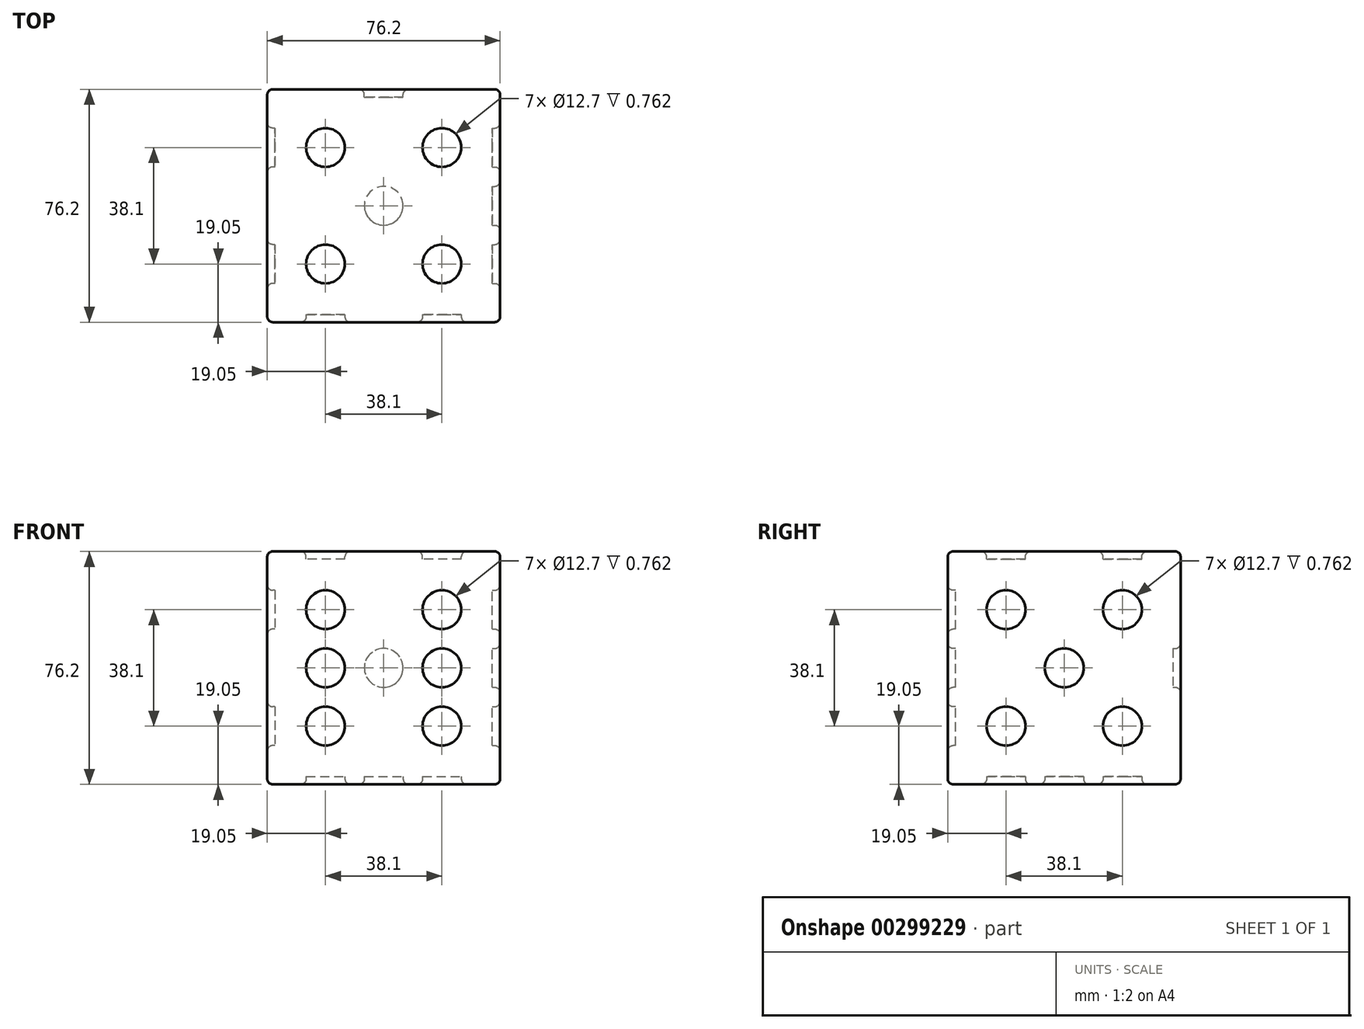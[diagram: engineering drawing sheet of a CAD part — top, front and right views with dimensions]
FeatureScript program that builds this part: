
annotation { "Feature Type Name" : "Feature", "Feature Type Description" : "" }
export const myFeature = defineFeature(function(context is Context, id is Id, definition is map)
    precondition{}
    {
        {
            var Q0;
            Q0=qCreatedBy(makeId("Top.planeOp"),FACE);
            var sketch = newSketch(context, id + "F0", { "sketchPlane" : qUnion([Q0])});
            skLineSegment(sketch, "E0.bottom", {"start": v(38.1, -38.1) * mm, "end": v(-38.1, -38.1) * mm});
            skLineSegment(sketch, "E0.top", {"start": v(38.1, 38.1) * mm, "end": v(-38.1, 38.1) * mm});
            skLineSegment(sketch, "E0.left", {"start": v(38.1, -38.1) * mm, "end": v(38.1, 38.1) * mm});
            skLineSegment(sketch, "E0.right", {"start": v(-38.1, -38.1) * mm, "end": v(-38.1, 38.1) * mm});
            skPoint(sketch, "E0.middle", {"position": v(0, 0) * mm});
            skSolve(sketch);
        }
        {
            var Q0;
            Q0 = qSketchRegion(id + "F0", true);
            extrude(context, id + "F1", {"entities" : qUnion([Q0]), "depth" : 38.1 * mm});
        }
        {
            var Q0;
            Q0 = qSketchRegion(id + "F0", true);
            extrude(context, id + "F2", {"entities" : qUnion([Q0]), "operationType" : NewBodyOperationType.ADD, "oppositeDirection" : true, "depth" : 38.1 * mm});
        }
        {
            var Q0;
            {var subQ0=sQuery(id+"F0.wireOp",EDGE,"E0.bottom");Q0=makeQuery(id+"F2.boolean.opBoolean","MERGE",FACE,{"derivedFrom":[makeQuery(id+"F1.opExtrude","SWEPT_FACE",FACE,{"disambiguationData":[OSD([subQ0])]}),makeQuery(id+"F2.opExtrude","SWEPT_FACE",FACE,{"disambiguationData":[OSD([subQ0])]})]});}
            var sketch = newSketch(context, id + "F3", { "sketchPlane" : qUnion([Q0])});
            skCircle(sketch, "E1", {"center": v(19.05, 19.05) * mm, "radius": 6.35 * mm});
            skCircle(sketch, "E2", {"center": v(-19.05, 19.05) * mm, "radius": 6.35 * mm});
            skCircle(sketch, "E3", {"center": v(-19.05, 0) * mm, "radius": 6.35 * mm});
            skCircle(sketch, "E4", {"center": v(19.05, 0) * mm, "radius": 6.35 * mm});
            skCircle(sketch, "E5", {"center": v(19.05, -19.05) * mm, "radius": 6.35 * mm});
            skCircle(sketch, "E6", {"center": v(-19.05, -19.05) * mm, "radius": 6.35 * mm});
            skSolve(sketch);
        }
        {
            var Q0;
            {var subQ0=sQuery(id+"F0.wireOp",EDGE,"E0.top");Q0=makeQuery(id+"F2.boolean.opBoolean","MERGE",FACE,{"derivedFrom":[makeQuery(id+"F1.opExtrude","SWEPT_FACE",FACE,{"disambiguationData":[OSD([subQ0])]}),makeQuery(id+"F2.opExtrude","SWEPT_FACE",FACE,{"disambiguationData":[OSD([subQ0])]})]});}
            var sketch = newSketch(context, id + "F4", { "sketchPlane" : qUnion([Q0])});
            skCircle(sketch, "E7", {"center": v(0, 0) * mm, "radius": 6.35 * mm});
            skSolve(sketch);
        }
        {
            var Q0;
            {var subQ0=sQuery(id+"F0.wireOp",EDGE,"E0.right");Q0=makeQuery(id+"F2.boolean.opBoolean","MERGE",FACE,{"derivedFrom":[makeQuery(id+"F1.opExtrude","SWEPT_FACE",FACE,{"disambiguationData":[OSD([subQ0])]}),makeQuery(id+"F2.opExtrude","SWEPT_FACE",FACE,{"disambiguationData":[OSD([subQ0])]})]});}
            var sketch = newSketch(context, id + "F5", { "sketchPlane" : qUnion([Q0])});
            skCircle(sketch, "E8", {"center": v(-19.05, 19.05) * mm, "radius": 6.35 * mm});
            skPoint(sketch, "E8.centerSnap0", {"position": v(0, 38.1) * mm});
            skCircle(sketch, "E9", {"center": v(19.05, -19.05) * mm, "radius": 6.35 * mm});
            skSolve(sketch);
        }
        {
            var Q0;
            {var subQ0=sQuery(id+"F0.wireOp",EDGE,"E0.left");Q0=makeQuery(id+"F2.boolean.opBoolean","MERGE",FACE,{"derivedFrom":[makeQuery(id+"F1.opExtrude","SWEPT_FACE",FACE,{"disambiguationData":[OSD([subQ0])]}),makeQuery(id+"F2.opExtrude","SWEPT_FACE",FACE,{"disambiguationData":[OSD([subQ0])]})]});}
            var sketch = newSketch(context, id + "F6", { "sketchPlane" : qUnion([Q0])});
            skCircle(sketch, "E10", {"center": v(19.05, 19.05) * mm, "radius": 6.35 * mm});
            skCircle(sketch, "E11", {"center": v(19.05, -19.05) * mm, "radius": 6.35 * mm});
            skCircle(sketch, "E12", {"center": v(0, 0) * mm, "radius": 6.35 * mm});
            skCircle(sketch, "E13", {"center": v(-19.05, -19.05) * mm, "radius": 6.35 * mm});
            skCircle(sketch, "E14", {"center": v(-19.05, 19.05) * mm, "radius": 6.35 * mm});
            skSolve(sketch);
        }
        {
            var Q0;
            Q0=makeQuery(id+"F2.opExtrude","CAP_FACE",FACE,{"disambiguationData":[OSD([sQuery(id+"F0.wireOp",EDGE,"E0.bottom"),sQuery(id+"F0.wireOp",EDGE,"E0.top"),sQuery(id+"F0.wireOp",EDGE,"E0.left"),sQuery(id+"F0.wireOp",EDGE,"E0.right")])],"isStart":false});
            var sketch = newSketch(context, id + "F7", { "sketchPlane" : qUnion([Q0])});
            skCircle(sketch, "E15", {"center": v(0, 0) * mm, "radius": 6.35 * mm});
            skCircle(sketch, "E16", {"center": v(-19.05, 19.05) * mm, "radius": 6.35 * mm});
            skCircle(sketch, "E17", {"center": v(19.05, -19.05) * mm, "radius": 6.35 * mm});
            skSolve(sketch);
        }
        {
            var Q0;
            Q0=makeQuery(id+"F1.opExtrude","CAP_FACE",FACE,{"disambiguationData":[OSD([sQuery(id+"F0.wireOp",EDGE,"E0.bottom"),sQuery(id+"F0.wireOp",EDGE,"E0.top"),sQuery(id+"F0.wireOp",EDGE,"E0.left"),sQuery(id+"F0.wireOp",EDGE,"E0.right")])],"isStart":false});
            var sketch = newSketch(context, id + "F8", { "sketchPlane" : qUnion([Q0])});
            skCircle(sketch, "E18", {"center": v(-19.05, -19.05) * mm, "radius": 6.35 * mm});
            skCircle(sketch, "E19", {"center": v(19.05, 19.05) * mm, "radius": 6.35 * mm});
            skCircle(sketch, "E20", {"center": v(-19.05, 19.05) * mm, "radius": 6.35 * mm});
            skCircle(sketch, "E21", {"center": v(19.05, -19.05) * mm, "radius": 6.35 * mm});
            skSolve(sketch);
        }
        {
            var Q0;
            Q0=makeQuery(id+"F8.imprint","IMPRINT",FACE,{"disambiguationData":[TD([[makeQuery(id+"F8.imprint","IMPRINT",EDGE,{"derivedFrom":sQuery(id+"F8.wireOp",EDGE,"E18")}),1.0]])]});
            var Q1;
            Q1=makeQuery(id+"F8.imprint","IMPRINT",FACE,{"disambiguationData":[TD([[makeQuery(id+"F8.imprint","IMPRINT",EDGE,{"derivedFrom":sQuery(id+"F8.wireOp",EDGE,"E19")}),1.0]])]});
            var Q2;
            Q2=makeQuery(id+"F8.imprint","IMPRINT",FACE,{"disambiguationData":[TD([[makeQuery(id+"F8.imprint","IMPRINT",EDGE,{"derivedFrom":sQuery(id+"F8.wireOp",EDGE,"E20")}),1.0]])]});
            var Q3;
            Q3=makeQuery(id+"F8.imprint","IMPRINT",FACE,{"disambiguationData":[TD([[makeQuery(id+"F8.imprint","IMPRINT",EDGE,{"derivedFrom":sQuery(id+"F8.wireOp",EDGE,"E21")}),1.0]])]});
            extrude(context, id + "F9", {"entities" : qUnion([Q0, Q1, Q2, Q3]), "operationType" : NewBodyOperationType.REMOVE, "oppositeDirection" : true, "depth" : 2.54 * mm});
        }
        {
            var Q0;
            Q0 = qSketchRegion(id + "F7", true);
            extrude(context, id + "F10", {"entities" : qUnion([Q0]), "operationType" : NewBodyOperationType.REMOVE, "oppositeDirection" : true, "depth" : 2.54 * mm});
        }
        {
            var Q0;
            Q0 = qSketchRegion(id + "F6", true);
            extrude(context, id + "F11", {"entities" : qUnion([Q0]), "operationType" : NewBodyOperationType.REMOVE, "oppositeDirection" : true, "depth" : 2.54 * mm});
        }
        {
            var Q0;
            Q0 = qSketchRegion(id + "F5", true);
            extrude(context, id + "F12", {"entities" : qUnion([Q0]), "operationType" : NewBodyOperationType.REMOVE, "oppositeDirection" : true, "depth" : 2.54 * mm});
        }
        {
            var Q0;
            Q0 = qSketchRegion(id + "F4", true);
            extrude(context, id + "F13", {"entities" : qUnion([Q0]), "operationType" : NewBodyOperationType.REMOVE, "oppositeDirection" : true, "depth" : 2.54 * mm});
        }
        {
            var Q0;
            Q0 = qSketchRegion(id + "F3", true);
            extrude(context, id + "F14", {"entities" : qUnion([Q0]), "operationType" : NewBodyOperationType.REMOVE, "oppositeDirection" : true, "depth" : 2.54 * mm});
        }
        {
            var Q0;
            Q0=makeQuery(id+"F2.opExtrude","CAP_FACE",FACE,{"disambiguationData":[OSD([sQuery(id+"F0.wireOp",EDGE,"E0.bottom"),sQuery(id+"F0.wireOp",EDGE,"E0.top"),sQuery(id+"F0.wireOp",EDGE,"E0.left"),sQuery(id+"F0.wireOp",EDGE,"E0.right")])],"isStart":false});
            var Q1;
            {var subQ0=sQuery(id+"F0.wireOp",EDGE,"E0.bottom");Q1=makeQuery(id+"F2.boolean.opBoolean","MERGE",FACE,{"derivedFrom":[makeQuery(id+"F1.opExtrude","SWEPT_FACE",FACE,{"disambiguationData":[OSD([subQ0])]}),makeQuery(id+"F2.opExtrude","SWEPT_FACE",FACE,{"disambiguationData":[OSD([subQ0])]})]});}
            var Q2;
            {var subQ0=sQuery(id+"F0.wireOp",EDGE,"E0.right");Q2=makeQuery(id+"F2.boolean.opBoolean","MERGE",FACE,{"derivedFrom":[makeQuery(id+"F1.opExtrude","SWEPT_FACE",FACE,{"disambiguationData":[OSD([subQ0])]}),makeQuery(id+"F2.opExtrude","SWEPT_FACE",FACE,{"disambiguationData":[OSD([subQ0])]})]});}
            var Q3;
            {var subQ0=sQuery(id+"F0.wireOp",EDGE,"E0.top");Q3=makeQuery(id+"F2.boolean.opBoolean","MERGE",FACE,{"derivedFrom":[makeQuery(id+"F1.opExtrude","SWEPT_FACE",FACE,{"disambiguationData":[OSD([subQ0])]}),makeQuery(id+"F2.opExtrude","SWEPT_FACE",FACE,{"disambiguationData":[OSD([subQ0])]})]});}
            var Q4;
            {var subQ0=sQuery(id+"F0.wireOp",EDGE,"E0.left");Q4=makeQuery(id+"F2.boolean.opBoolean","MERGE",FACE,{"derivedFrom":[makeQuery(id+"F1.opExtrude","SWEPT_FACE",FACE,{"disambiguationData":[OSD([subQ0])]}),makeQuery(id+"F2.opExtrude","SWEPT_FACE",FACE,{"disambiguationData":[OSD([subQ0])]})]});}
            var Q5;
            Q5=makeQuery(id+"F1.opExtrude","CAP_FACE",FACE,{"disambiguationData":[OSD([sQuery(id+"F0.wireOp",EDGE,"E0.bottom"),sQuery(id+"F0.wireOp",EDGE,"E0.top"),sQuery(id+"F0.wireOp",EDGE,"E0.left"),sQuery(id+"F0.wireOp",EDGE,"E0.right")])],"isStart":false});
            fillet(context, id + "F15", {"entities" : qUnion([Q0, Q1, Q2, Q3, Q4, Q5]), "radius" : 1.78 * mm, "tangentPropagation" : true, "allowEdgeOverflow" : false});
        }
    });
